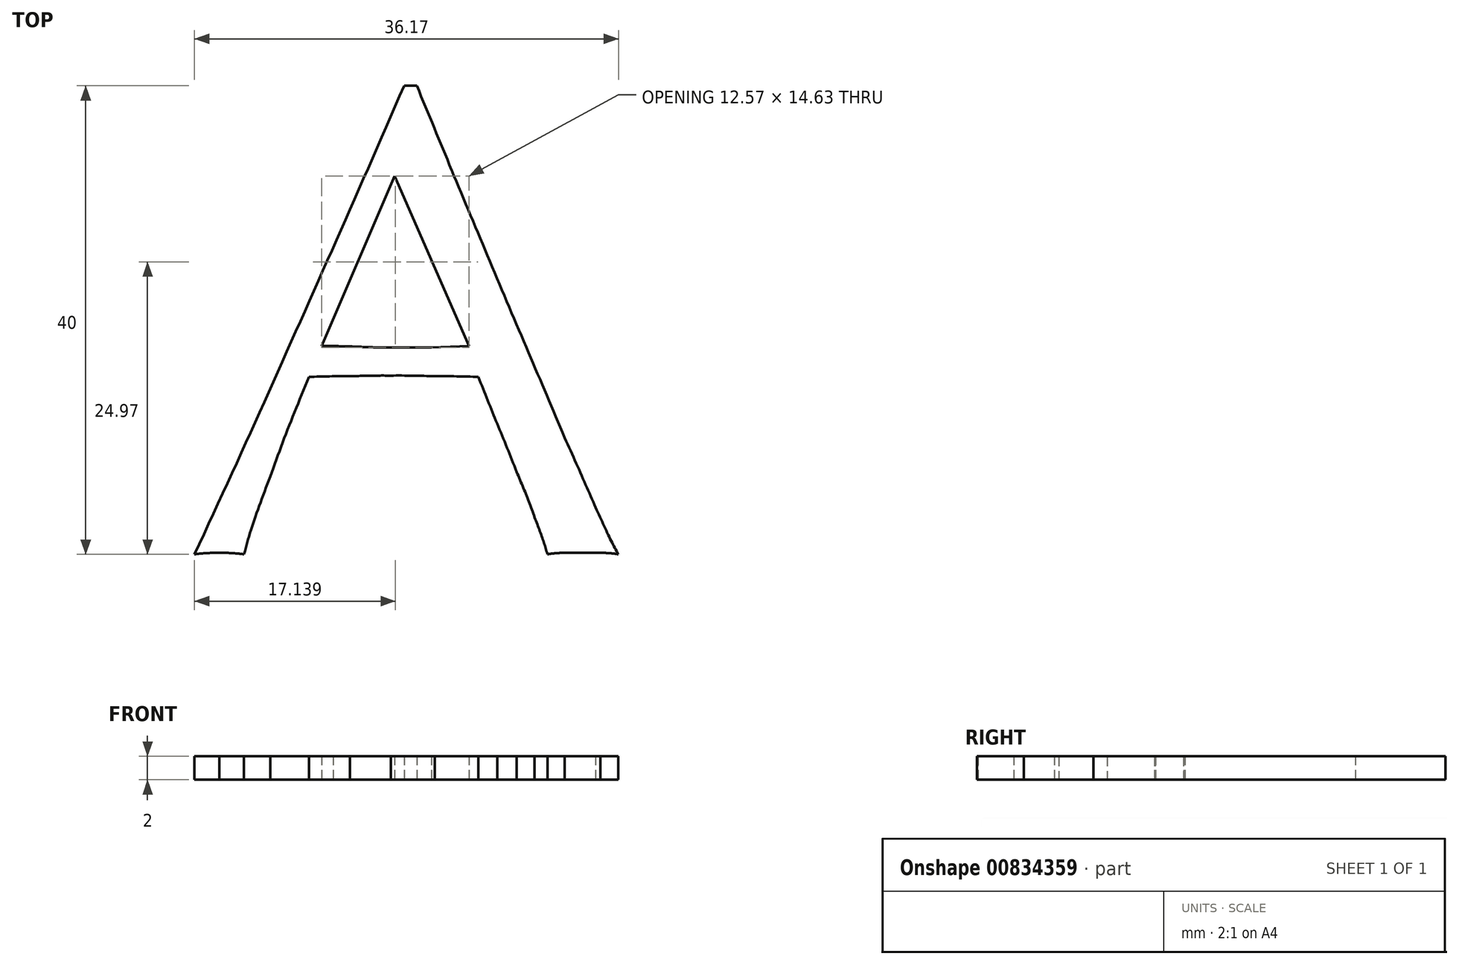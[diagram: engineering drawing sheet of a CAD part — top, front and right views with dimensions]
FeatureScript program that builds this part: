
annotation { "Feature Type Name" : "Feature", "Feature Type Description" : "" }
export const myFeature = defineFeature(function(context is Context, id is Id, definition is map)
    precondition{}
    {
        {
            var Q0;
            Q0=qCreatedBy(makeId("Top.planeOp"),FACE);
            var sketch = newSketch(context, id + "F0", { "sketchPlane" : qUnion([Q0])});
            skLineSegment(sketch, "E0", {"start": v(-3.95, 18.4) * mm, "end": v(-4.17, 9.83) * mm});
            skLineSegment(sketch, "E1", {"start": v(-4.17, 9.83) * mm, "end": v(-3.95, 18.4) * mm});
            skLineSegment(sketch, "E2", {"start": v(-18.06, 28.57) * mm, "end": v(-18.06, 25.6) * mm});
            skLineSegment(sketch, "E3", {"start": v(-18.06, 25.6) * mm, "end": v(-17.43, 25.6) * mm});
            skLineSegment(sketch, "E4", {"start": v(-17.43, 25.6) * mm, "end": v(-18.06, 28.57) * mm});
            skLineSegment(sketch, "E5", {"start": v(3.6, 4.86) * mm, "end": v(3.6, 6.11) * mm});
            skLineSegment(sketch, "E6", {"start": v(3.6, 6.11) * mm, "end": v(3.6, 4.86) * mm});
            skLineSegment(sketch, "E7", {"start": v(22.91, 26.63) * mm, "end": v(23.31, 26.91) * mm});
            skLineSegment(sketch, "E8", {"start": v(23.31, 26.91) * mm, "end": v(22.91, 26.63) * mm});
            skLineSegment(sketch, "E9", {"start": v(14.34, 25.71) * mm, "end": v(14.23, 25.77) * mm});
            skLineSegment(sketch, "E10", {"start": v(14.23, 25.77) * mm, "end": v(14.34, 25.71) * mm});
            skLineSegment(sketch, "E11", {"start": v(10.06, 19.49) * mm, "end": v(10.06, 17.66) * mm});
            skLineSegment(sketch, "E12", {"start": v(10.06, 17.66) * mm, "end": v(10.06, 19.49) * mm});
            skLineSegment(sketch, "E13", {"start": v(14.29, 13.31) * mm, "end": v(14.29, 19.6) * mm});
            skLineSegment(sketch, "E14", {"start": v(14.29, 19.6) * mm, "end": v(14.29, 13.31) * mm});
            skLineSegment(sketch, "E15", {"start": v(6.2, -28.25) * mm, "end": v(-0.14, -13.73) * mm});
            skLineSegment(sketch, "E16", {"start": v(-0.14, -13.73) * mm, "end": v(-6.37, -28.25) * mm});
            skLineSegment(sketch, "E17", {"start": v(-6.37, -28.25) * mm, "end": v(6.2, -28.25) * mm});
            skLineSegment(sketch, "E18", {"start": v(0.66, -6.02) * mm, "end": v(1.75, -6.02) * mm});
            skLineSegment(sketch, "E19", {"start": v(1.75, -6.02) * mm, "end": v(0.66, -6.02) * mm});
            skFitSpline(sketch, "E20", {"points": [v(-4.17, 9.83) * mm, v(-4.82, 8.76) * mm, v(-5.75, 7.83) * mm, v(-6.97, 7.03) * mm]});
            skFitSpline(sketch, "E21", {"points": [v(-6.97, 7.03) * mm, v(-8.15, 6.23) * mm, v(-9.47, 5.83) * mm, v(-10.92, 5.83) * mm]});
            skFitSpline(sketch, "E22", {"points": [v(-10.92, 5.83) * mm, v(-12.17, 5.83) * mm, v(-13.32, 6.29) * mm, v(-14.35, 7.2) * mm]});
            skFitSpline(sketch, "E23", {"points": [v(-14.35, 7.2) * mm, v(-15.37, 8.11) * mm, v(-15.89, 9.47) * mm, v(-15.89, 11.26) * mm]});
            skFitSpline(sketch, "E24", {"points": [v(-15.89, 11.26) * mm, v(-15.89, 12.32) * mm, v(-15.7, 13.2) * mm, v(-15.32, 13.89) * mm]});
            skFitSpline(sketch, "E25", {"points": [v(-15.32, 13.89) * mm, v(-14.9, 14.57) * mm, v(-14.36, 15.14) * mm, v(-13.72, 15.6) * mm]});
            skFitSpline(sketch, "E26", {"points": [v(-13.72, 15.6) * mm, v(-13.03, 16.06) * mm, v(-12.27, 16.42) * mm, v(-11.43, 16.69) * mm]});
            skFitSpline(sketch, "E27", {"points": [v(-11.43, 16.69) * mm, v(-10.55, 16.95) * mm, v(-9.68, 17.16) * mm, v(-8.8, 17.31) * mm]});
            skFitSpline(sketch, "E28", {"points": [v(-8.8, 17.31) * mm, v(-7.93, 17.5) * mm, v(-7.07, 17.68) * mm, v(-6.23, 17.83) * mm]});
            skFitSpline(sketch, "E29", {"points": [v(-6.23, 17.83) * mm, v(-5.35, 17.98) * mm, v(-4.6, 18.17) * mm, v(-3.95, 18.4) * mm]});
            skFitSpline(sketch, "E30", {"points": [v(-17.43, 25.6) * mm, v(-16.78, 26.82) * mm, v(-15.81, 27.77) * mm, v(-14.52, 28.46) * mm]});
            skFitSpline(sketch, "E31", {"points": [v(-14.52, 28.46) * mm, v(-13.18, 29.14) * mm, v(-11.75, 29.49) * mm, v(-10.23, 29.49) * mm]});
            skFitSpline(sketch, "E32", {"points": [v(-10.23, 29.49) * mm, v(-9.09, 29.49) * mm, v(-8.12, 29.28) * mm, v(-7.32, 28.86) * mm]});
            skFitSpline(sketch, "E33", {"points": [v(-7.32, 28.86) * mm, v(-6.52, 28.48) * mm, v(-5.87, 27.96) * mm, v(-5.37, 27.31) * mm]});
            skFitSpline(sketch, "E34", {"points": [v(-5.37, 27.31) * mm, v(-4.88, 26.67) * mm, v(-4.52, 25.9) * mm, v(-4.29, 25.03) * mm]});
            skFitSpline(sketch, "E35", {"points": [v(-4.29, 25.03) * mm, v(-4.06, 24.15) * mm, v(-3.95, 23.24) * mm, v(-3.95, 22.29) * mm]});
            skFitSpline(sketch, "E36", {"points": [v(-3.95, 22.29) * mm, v(-3.95, 21.71) * mm, v(-4, 21.24) * mm, v(-4.12, 20.86) * mm]});
            skFitSpline(sketch, "E37", {"points": [v(-4.12, 20.86) * mm, v(-4.23, 20.51) * mm, v(-4.57, 20.21) * mm, v(-5.15, 19.94) * mm]});
            skFitSpline(sketch, "E38", {"points": [v(-5.15, 19.94) * mm, v(-5.68, 19.68) * mm, v(-6.54, 19.41) * mm, v(-7.72, 19.14) * mm]});
            skFitSpline(sketch, "E39", {"points": [v(-7.72, 19.14) * mm, v(-8.86, 18.91) * mm, v(-10.46, 18.63) * mm, v(-12.52, 18.29) * mm]});
            skFitSpline(sketch, "E40", {"points": [v(-12.52, 18.29) * mm, v(-15.03, 17.87) * mm, v(-17.01, 17.03) * mm, v(-18.46, 15.77) * mm]});
            skFitSpline(sketch, "E41", {"points": [v(-18.46, 15.77) * mm, v(-19.87, 14.51) * mm, v(-20.57, 12.74) * mm, v(-20.57, 10.46) * mm]});
            skFitSpline(sketch, "E42", {"points": [v(-20.57, 10.46) * mm, v(-20.57, 9.35) * mm, v(-20.36, 8.36) * mm, v(-19.95, 7.49) * mm]});
            skFitSpline(sketch, "E43", {"points": [v(-19.95, 7.49) * mm, v(-19.49, 6.65) * mm, v(-18.92, 5.92) * mm, v(-18.23, 5.31) * mm]});
            skFitSpline(sketch, "E44", {"points": [v(-18.23, 5.31) * mm, v(-17.5, 4.7) * mm, v(-16.69, 4.27) * mm, v(-15.77, 4) * mm]});
            skFitSpline(sketch, "E45", {"points": [v(-15.77, 4) * mm, v(-14.86, 3.73) * mm, v(-13.93, 3.6) * mm, v(-12.97, 3.6) * mm]});
            skFitSpline(sketch, "E46", {"points": [v(-12.97, 3.6) * mm, v(-11.03, 3.6) * mm, v(-9.4, 3.92) * mm, v(-8.06, 4.57) * mm]});
            skFitSpline(sketch, "E47", {"points": [v(-8.06, 4.57) * mm, v(-6.73, 5.22) * mm, v(-5.37, 6.23) * mm, v(-4, 7.6) * mm]});
            skFitSpline(sketch, "E48", {"points": [v(-4, 7.6) * mm, v(-3.89, 6.61) * mm, v(-3.5, 5.8) * mm, v(-2.86, 5.14) * mm]});
            skFitSpline(sketch, "E49", {"points": [v(-2.86, 5.14) * mm, v(-2.21, 4.53) * mm, v(-1.28, 4.23) * mm, v(-0.06, 4.23) * mm]});
            skFitSpline(sketch, "E50", {"points": [v(-0.06, 4.23) * mm, v(0.7, 4.23) * mm, v(1.39, 4.29) * mm, v(2, 4.4) * mm]});
            skFitSpline(sketch, "E51", {"points": [v(2, 4.4) * mm, v(2.65, 4.51) * mm, v(3.18, 4.67) * mm, v(3.6, 4.86) * mm]});
            skFitSpline(sketch, "E52", {"points": [v(3.6, 6.11) * mm, v(3.4, 6) * mm, v(3.2, 5.92) * mm, v(2.97, 5.89) * mm]});
            skFitSpline(sketch, "E53", {"points": [v(2.97, 5.89) * mm, v(2.78, 5.89) * mm, v(2.59, 5.89) * mm, v(2.4, 5.89) * mm]});
            skFitSpline(sketch, "E54", {"points": [v(2.4, 5.89) * mm, v(1.83, 5.89) * mm, v(1.39, 6.02) * mm, v(1.08, 6.29) * mm]});
            skFitSpline(sketch, "E55", {"points": [v(1.08, 6.29) * mm, v(0.82, 6.55) * mm, v(0.6, 6.88) * mm, v(0.45, 7.26) * mm]});
            skFitSpline(sketch, "E56", {"points": [v(0.45, 7.26) * mm, v(0.3, 7.68) * mm, v(0.2, 8.13) * mm, v(0.17, 8.63) * mm]});
            skFitSpline(sketch, "E57", {"points": [v(0.17, 8.63) * mm, v(0.17, 9.16) * mm, v(0.17, 9.66) * mm, v(0.17, 10.11) * mm]});
            skFitSpline(sketch, "E58", {"points": [v(0.17, 10.11) * mm, v(0.17, 12.51) * mm, v(0.2, 14.78) * mm, v(0.28, 16.91) * mm]});
            skFitSpline(sketch, "E59", {"points": [v(0.28, 16.91) * mm, v(0.36, 19.09) * mm, v(0.4, 21.26) * mm, v(0.4, 23.43) * mm]});
            skFitSpline(sketch, "E60", {"points": [v(0.4, 23.43) * mm, v(0.4, 24.69) * mm, v(0.17, 25.83) * mm, v(-0.29, 26.86) * mm]});
            skFitSpline(sketch, "E61", {"points": [v(-0.29, 26.86) * mm, v(-0.75, 27.92) * mm, v(-1.37, 28.82) * mm, v(-2.17, 29.54) * mm]});
            skFitSpline(sketch, "E62", {"points": [v(-2.17, 29.54) * mm, v(-2.97, 30.3) * mm, v(-3.95, 30.88) * mm, v(-5.09, 31.26) * mm]});
            skFitSpline(sketch, "E63", {"points": [v(-5.09, 31.26) * mm, v(-6.23, 31.68) * mm, v(-7.49, 31.89) * mm, v(-8.86, 31.89) * mm]});
            skFitSpline(sketch, "E64", {"points": [v(-8.86, 31.89) * mm, v(-10.38, 31.89) * mm, v(-11.87, 31.66) * mm, v(-13.32, 31.2) * mm]});
            skFitSpline(sketch, "E65", {"points": [v(-13.32, 31.2) * mm, v(-14.76, 30.74) * mm, v(-16.35, 29.87) * mm, v(-18.06, 28.57) * mm]});
            skFitSpline(sketch, "E66", {"points": [v(23.31, 26.91) * mm, v(23.31, 27.68) * mm, v(23.33, 28.51) * mm, v(23.37, 29.43) * mm]});
            skFitSpline(sketch, "E67", {"points": [v(23.37, 29.43) * mm, v(23.4, 30.38) * mm, v(23.52, 31.09) * mm, v(23.71, 31.54) * mm]});
            skFitSpline(sketch, "E68", {"points": [v(23.71, 31.54) * mm, v(23.33, 31.7) * mm, v(23, 31.8) * mm, v(22.74, 31.83) * mm]});
            skFitSpline(sketch, "E69", {"points": [v(22.74, 31.83) * mm, v(22.51, 31.87) * mm, v(22.23, 31.89) * mm, v(21.89, 31.89) * mm]});
            skFitSpline(sketch, "E70", {"points": [v(21.89, 31.89) * mm, v(19.1, 31.89) * mm, v(16.6, 29.83) * mm, v(14.34, 25.71) * mm]});
            skFitSpline(sketch, "E71", {"points": [v(14.23, 25.77) * mm, v(14.23, 26.5) * mm, v(14.23, 27.26) * mm, v(14.23, 28.06) * mm]});
            skFitSpline(sketch, "E72", {"points": [v(14.23, 28.06) * mm, v(14.27, 28.86) * mm, v(14.36, 29.94) * mm, v(14.51, 31.31) * mm]});
            skFitSpline(sketch, "E73", {"points": [v(14.51, 31.31) * mm, v(14.1, 31.24) * mm, v(13.7, 31.16) * mm, v(13.31, 31.09) * mm]});
            skFitSpline(sketch, "E74", {"points": [v(13.31, 31.09) * mm, v(12.93, 31.05) * mm, v(12.57, 31.03) * mm, v(12.23, 31.03) * mm]});
            skFitSpline(sketch, "E75", {"points": [v(12.23, 31.03) * mm, v(11.8, 31.03) * mm, v(11.4, 31.05) * mm, v(11.03, 31.09) * mm]});
            skFitSpline(sketch, "E76", {"points": [v(11.03, 31.09) * mm, v(10.65, 31.16) * mm, v(10.25, 31.24) * mm, v(9.83, 31.31) * mm]});
            skFitSpline(sketch, "E77", {"points": [v(9.83, 31.31) * mm, v(9.94, 28.8) * mm, v(10, 26.57) * mm, v(10, 24.63) * mm]});
            skFitSpline(sketch, "E78", {"points": [v(10, 24.63) * mm, v(10.04, 22.69) * mm, v(10.06, 20.97) * mm, v(10.06, 19.49) * mm]});
            skFitSpline(sketch, "E79", {"points": [v(10.06, 17.66) * mm, v(10.06, 14.42) * mm, v(10.04, 11.68) * mm, v(10, 9.43) * mm]});
            skFitSpline(sketch, "E80", {"points": [v(10, 9.43) * mm, v(10, 7.22) * mm, v(9.94, 5.47) * mm, v(9.83, 4.17) * mm]});
            skFitSpline(sketch, "E81", {"points": [v(9.83, 4.17) * mm, v(10.6, 4.25) * mm, v(11.4, 4.29) * mm, v(12.23, 4.29) * mm]});
            skFitSpline(sketch, "E82", {"points": [v(12.23, 4.29) * mm, v(13, 4.29) * mm, v(13.75, 4.25) * mm, v(14.51, 4.17) * mm]});
            skFitSpline(sketch, "E83", {"points": [v(14.51, 4.17) * mm, v(14.4, 5.01) * mm, v(14.32, 6.1) * mm, v(14.29, 7.43) * mm]});
            skFitSpline(sketch, "E84", {"points": [v(14.29, 7.43) * mm, v(14.29, 8.8) * mm, v(14.29, 10.76) * mm, v(14.29, 13.31) * mm]});
            skFitSpline(sketch, "E85", {"points": [v(14.29, 19.6) * mm, v(14.29, 20.7) * mm, v(14.42, 21.73) * mm, v(14.69, 22.69) * mm]});
            skFitSpline(sketch, "E86", {"points": [v(14.69, 22.69) * mm, v(14.95, 23.68) * mm, v(15.33, 24.51) * mm, v(15.83, 25.2) * mm]});
            skFitSpline(sketch, "E87", {"points": [v(15.83, 25.2) * mm, v(16.32, 25.92) * mm, v(16.93, 26.5) * mm, v(17.66, 26.91) * mm]});
            skFitSpline(sketch, "E88", {"points": [v(17.66, 26.91) * mm, v(18.38, 27.33) * mm, v(19.2, 27.54) * mm, v(20.11, 27.54) * mm]});
            skFitSpline(sketch, "E89", {"points": [v(20.11, 27.54) * mm, v(20.69, 27.54) * mm, v(21.24, 27.45) * mm, v(21.77, 27.26) * mm]});
            skFitSpline(sketch, "E90", {"points": [v(21.77, 27.26) * mm, v(22.34, 27.07) * mm, v(22.72, 26.86) * mm, v(22.91, 26.63) * mm]});
            skFitSpline(sketch, "E91", {"points": [v(-6.37, -28.25) * mm, v(-5.38, -28.25) * mm, v(-4.35, -28.27) * mm, v(-3.28, -28.3) * mm]});
            skFitSpline(sketch, "E92", {"points": [v(-3.28, -28.3) * mm, v(-2.21, -28.34) * mm, v(-1.19, -28.36) * mm, v(-0.2, -28.36) * mm]});
            skFitSpline(sketch, "E93", {"points": [v(-0.2, -28.36) * mm, v(0.87, -28.36) * mm, v(1.94, -28.36) * mm, v(3, -28.36) * mm]});
            skFitSpline(sketch, "E94", {"points": [v(3, -28.36) * mm, v(4.07, -28.33) * mm, v(5.14, -28.29) * mm, v(6.2, -28.25) * mm]});
            skFitSpline(sketch, "E95", {"points": [v(18.95, -46.02) * mm, v(18.41, -45.94) * mm, v(17.9, -45.9) * mm, v(17.4, -45.9) * mm]});
            skFitSpline(sketch, "E96", {"points": [v(17.4, -45.9) * mm, v(16.95, -45.9) * mm, v(16.45, -45.9) * mm, v(15.92, -45.9) * mm]});
            skFitSpline(sketch, "E97", {"points": [v(15.92, -45.9) * mm, v(15.39, -45.9) * mm, v(14.87, -45.9) * mm, v(14.38, -45.9) * mm]});
            skFitSpline(sketch, "E98", {"points": [v(14.38, -45.9) * mm, v(13.92, -45.9) * mm, v(13.42, -45.94) * mm, v(12.9, -46.02) * mm]});
            skFitSpline(sketch, "E99", {"points": [v(12.9, -46.02) * mm, v(12.62, -45.14) * mm, v(12.26, -44.1) * mm, v(11.8, -42.88) * mm]});
            skFitSpline(sketch, "E100", {"points": [v(11.8, -42.88) * mm, v(11.35, -41.62) * mm, v(10.83, -40.33) * mm, v(10.26, -39) * mm]});
            skFitSpline(sketch, "E101", {"points": [v(10.26, -39) * mm, v(9.73, -37.62) * mm, v(9.18, -36.25) * mm, v(8.6, -34.88) * mm]});
            skFitSpline(sketch, "E102", {"points": [v(8.6, -34.88) * mm, v(8.03, -33.47) * mm, v(7.5, -32.13) * mm, v(7, -30.88) * mm]});
            skFitSpline(sketch, "E103", {"points": [v(7, -30.88) * mm, v(5.79, -30.84) * mm, v(4.55, -30.82) * mm, v(3.3, -30.82) * mm]});
            skFitSpline(sketch, "E104", {"points": [v(3.3, -30.82) * mm, v(2.03, -30.78) * mm, v(0.78, -30.76) * mm, v(-0.48, -30.76) * mm]});
            skFitSpline(sketch, "E105", {"points": [v(-0.48, -30.76) * mm, v(-1.66, -30.76) * mm, v(-2.82, -30.78) * mm, v(-3.97, -30.82) * mm]});
            skFitSpline(sketch, "E106", {"points": [v(-3.97, -30.82) * mm, v(-5.1, -30.82) * mm, v(-6.27, -30.84) * mm, v(-7.45, -30.88) * mm]});
            skFitSpline(sketch, "E107", {"points": [v(-7.45, -30.88) * mm, v(-8.67, -33.85) * mm, v(-9.78, -36.69) * mm, v(-10.77, -39.4) * mm]});
            skFitSpline(sketch, "E108", {"points": [v(-10.77, -39.4) * mm, v(-11.76, -42.06) * mm, v(-12.5, -44.27) * mm, v(-13, -46.02) * mm]});
            skFitSpline(sketch, "E109", {"points": [v(-13, -46.02) * mm, v(-13.64, -45.94) * mm, v(-14.35, -45.9) * mm, v(-15.1, -45.9) * mm]});
            skFitSpline(sketch, "E110", {"points": [v(-15.1, -45.9) * mm, v(-15.87, -45.9) * mm, v(-16.58, -45.94) * mm, v(-17.22, -46.02) * mm]});
            skFitSpline(sketch, "E111", {"points": [v(-17.22, -46.02) * mm, v(-14.14, -39.35) * mm, v(-11.13, -32.73) * mm, v(-8.2, -26.13) * mm]});
            skFitSpline(sketch, "E112", {"points": [v(-8.2, -26.13) * mm, v(-5.26, -19.54) * mm, v(-2.3, -12.84) * mm, v(0.66, -6.02) * mm]});
            skFitSpline(sketch, "E113", {"points": [v(1.75, -6.02) * mm, v(2.66, -8.23) * mm, v(3.65, -10.63) * mm, v(4.72, -13.22) * mm]});
            skFitSpline(sketch, "E114", {"points": [v(4.72, -13.22) * mm, v(5.79, -15.77) * mm, v(6.87, -18.36) * mm, v(7.98, -21) * mm]});
            skFitSpline(sketch, "E115", {"points": [v(7.98, -21) * mm, v(9.08, -23.62) * mm, v(10.19, -26.23) * mm, v(11.3, -28.82) * mm]});
            skFitSpline(sketch, "E116", {"points": [v(11.3, -28.82) * mm, v(12.4, -31.41) * mm, v(13.42, -33.83) * mm, v(14.38, -36.08) * mm]});
            skFitSpline(sketch, "E117", {"points": [v(14.38, -36.08) * mm, v(15.37, -38.29) * mm, v(16.24, -40.27) * mm, v(17, -42.02) * mm]});
            skFitSpline(sketch, "E118", {"points": [v(17, -42.02) * mm, v(17.8, -43.77) * mm, v(18.45, -45.1) * mm, v(18.95, -46.02) * mm]});
            skSolve(sketch);
        }
        {
            var Q0;
            Q0=makeQuery(id+"F0.imprint","IMPRINT",FACE,{"disambiguationData":[TD([[makeQuery(id+"F0.imprint","IMPRINT",EDGE,{"derivedFrom":sQuery(id+"F0.wireOp",EDGE,"E15")}),-1.0]])]});
            var Q1;
            Q1=makeQuery(id+"F0.imprint","IMPRINT",FACE,{"disambiguationData":[TD([[makeQuery(id+"F0.imprint","IMPRINT",EDGE,{"derivedFrom":sQuery(id+"F0.wireOp",EDGE,"E1")}),-1.0]])]});
            var Q2;
            Q2=makeQuery(id+"F0.imprint","IMPRINT",FACE,{"disambiguationData":[TD([[makeQuery(id+"F0.imprint","IMPRINT",EDGE,{"derivedFrom":sQuery(id+"F0.wireOp",EDGE,"E8")}),-1.0]])]});
            extrude(context, id + "F1", {"entities" : qUnion([Q0, Q1, Q2]), "depth" : 2 * mm, "offsetDistance" : 25 * mm});
        }
    });
